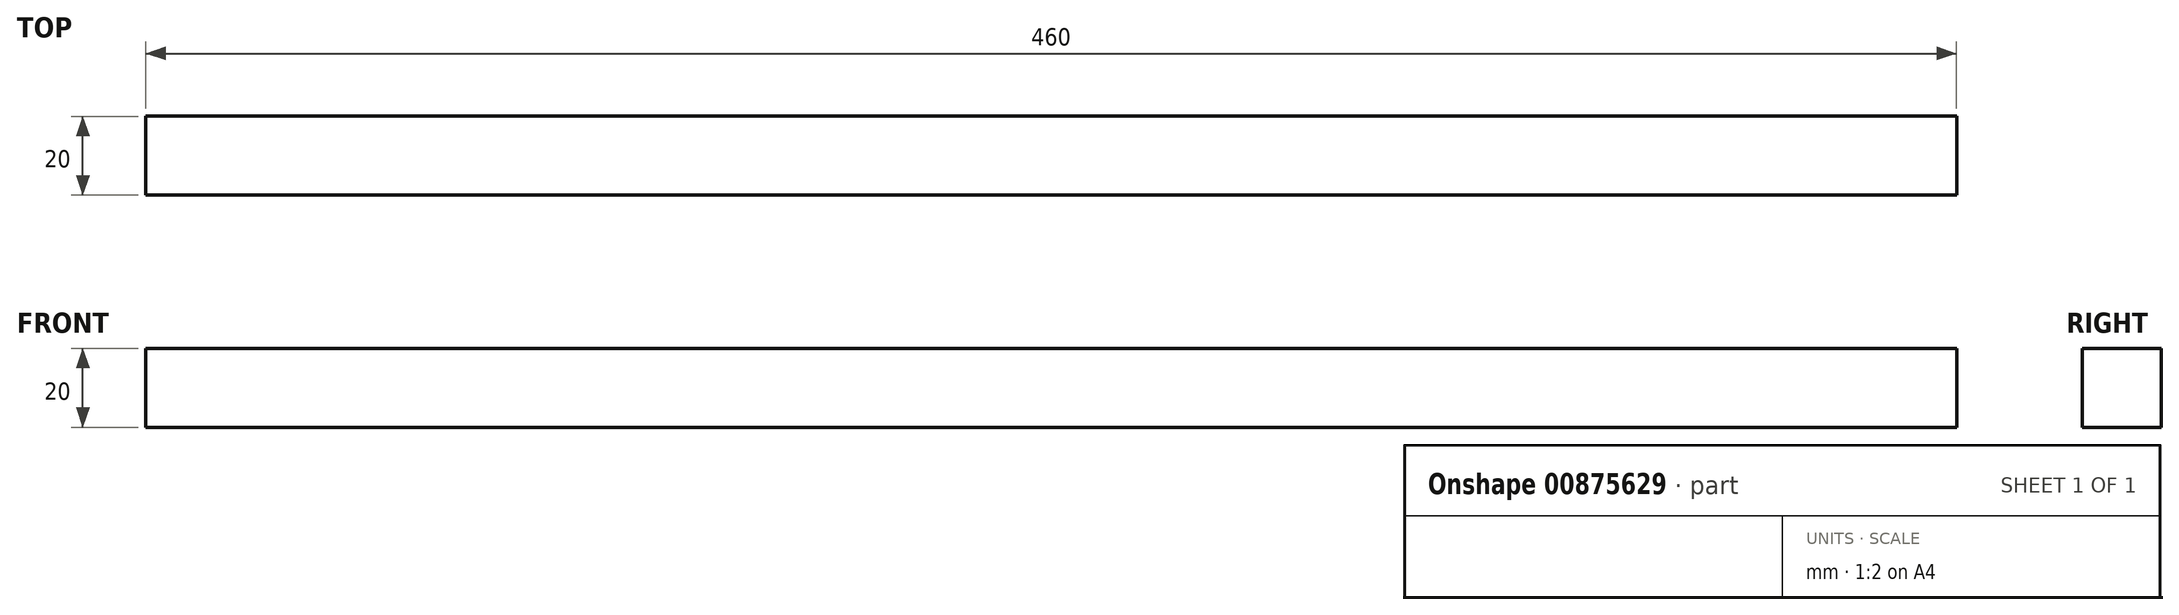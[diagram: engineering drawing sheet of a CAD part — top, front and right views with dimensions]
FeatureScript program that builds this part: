
annotation { "Feature Type Name" : "Feature", "Feature Type Description" : "" }
export const myFeature = defineFeature(function(context is Context, id is Id, definition is map)
    precondition{}
    {
        {
            var Q0;
            Q0=qCreatedBy(makeId("Top.planeOp"),FACE);
            var sketch = newSketch(context, id + "F0", { "sketchPlane" : qUnion([Q0])});
            skLineSegment(sketch, "E0.bottom", {"start": v(-22.24, 15) * mm, "end": v(437.76, 15) * mm});
            skLineSegment(sketch, "E0.top", {"start": v(-22.24, -5) * mm, "end": v(437.76, -5) * mm});
            skLineSegment(sketch, "E0.left", {"start": v(-22.24, 15) * mm, "end": v(-22.24, -5) * mm});
            skLineSegment(sketch, "E0.right", {"start": v(437.76, 15) * mm, "end": v(437.76, -5) * mm});
            skSolve(sketch);
        }
        {
            var Q0;
            Q0=makeQuery(id+"F0.imprint","IMPRINT",FACE,{"disambiguationData":[TD([[makeQuery(id+"F0.imprint","IMPRINT",EDGE,{"derivedFrom":sQuery(id+"F0.wireOp",EDGE,"E0.bottom")}),-1.0]])]});
            extrude(context, id + "F1", {"entities" : qUnion([Q0]), "depth" : 20 * mm, "offsetDistance" : 25 * mm});
        }
        {
            var Q0;
            Q0=qCreatedBy(makeId("Top.planeOp"),FACE);
            var sketch = newSketch(context, id + "F2", { "sketchPlane" : qUnion([Q0])});
            skLineSegment(sketch, "E1.bottom", {"start": v(-116.79, 226.75) * mm, "end": v(-96.79, 226.75) * mm});
            skLineSegment(sketch, "E1.top", {"start": v(-116.79, -73.25) * mm, "end": v(-96.79, -73.25) * mm});
            skLineSegment(sketch, "E1.left", {"start": v(-116.79, 226.75) * mm, "end": v(-116.79, -73.25) * mm});
            skLineSegment(sketch, "E1.right", {"start": v(-96.79, 226.75) * mm, "end": v(-96.79, -73.25) * mm});
            skSolve(sketch);
        }
        {
            var Q0;
            Q0=makeQuery(id+"F2.imprint","IMPRINT",FACE,{"disambiguationData":[TD([[makeQuery(id+"F2.imprint","IMPRINT",EDGE,{"derivedFrom":sQuery(id+"F2.wireOp",EDGE,"E1.bottom")}),-1.0]])]});
            extrude(context, id + "F3", {"entities" : qUnion([Q0]), "depth" : 20 * mm, "offsetDistance" : 25 * mm});
        }
        {
            var Q0;
            Q0=makeQuery(id+"F3.opExtrude","SWEPT_BODY",BODY,{"disambiguationData":[OSD([sQuery(id+"F2.wireOp",EDGE,"E1.bottom"),sQuery(id+"F2.wireOp",EDGE,"E1.top"),sQuery(id+"F2.wireOp",EDGE,"E1.left"),sQuery(id+"F2.wireOp",EDGE,"E1.right")])]});
            deleteBodies(context, id + "F4", {"entities" : qUnion([Q0])});
        }
    });
